# Revit family: ISI_IdealStandard_CounterTopWashbasins_Strada
name_source: partatom
category: Plumbing Fixtures
revit_build: Autodesk Revit MEP 2012 (Build: 20110309_2315(x64)
units: mm (PartAtom-declared; Revit-internal decimal feet)

## types (3) — shared parameters
Accessories = www.idealspec.co.uk
AreaUnits = millimeters
Assembly Code = C1030220
AssetType = Fixed
BREEAM = No
BasinMaterial = ISI_IdealStandard_Sanitaryware_White6_Render
Brand = Ideal Standard
Category = SanitaryTerminal_WASHHANDBASIN_UK
Color = White
ConnectionType = Plumbing
Default Elevation = 1219 mm
DrainSize = 32 mm  [stored 0.104987 ft]
DurationUnit = year
ECA = No
ExpectedLife = 30
Features = Single tap hole, overflow, contemporary design
Finish = White
IfcExportAs = IfcSanitaryTerminalType
IfcExportType = WASHHANDBASIN
InstallationInstructions = www.idealspec.co.uk/resources.html
LinearUnits = millimeters
ManufacturerURL = www.idealspec.co.uk
Material = Vitreous china
NBSDescription = Counter top washbasins
NBSReference = 45-35-70/360
NominalHeight = 130 mm  [stored 0.426509 ft]
NominalWidth = 420 mm
Shape = Rectangular
Space = Internal
SpareParts = www.fastpart-spares.co.uk
TMV3 = No
URL = www.idealspec.co.uk
Uniclass2 = Pr_40_20_96_18
Version = 2
VolumeUnits = Litres
WRAS = No
WarrantyDescription = Manufacturers Warranty
WarrantyDurationParts = 99
WarrantyDurationUnit = year
WashHandBasinMounting = CounterTop
WashHandBasinType = HandRinse
WaterEfficientProduct = No
zero-valued in all types: CWFU, HWFU, WFU

## per-type parameters (varying)
| type | BIMObjectName | Description | Model | ModelNumber | ModelReference | Name | NettWeight | NominalDepth | NominalLength | ProductInformation | Size | WasteCentreLine |
| K077701 - Ideal Standard Strada 50cm Countertop Basin | ISI_IdealStandard_CounterTopWashbasins_Strada_K0777 | Strada 50 cm countertop basin one taphole | K077701 | K077701 | Strada 50 cm countertop basin one taphole | CounterTopWashBasins_Strada_K0777_IdealStandard | 13 Kg | 500 mm | 500 mm | www.idealspec.co.uk/assets/datasheet/K077701 | 500 x 420 x 145 mm | 210 mm |
| K077801 - Ideal Standard Strada 60cm Countertop Basin | ISI_IdealStandard_CounterTopWashbasins_Strada_K0778 | Strada 60 cm countertop basin one taphole | K077801 | K077801 | Strada 60 cm countertop basin one taphole | CounterTopWashBasins_Strada_K0778_IdealStandard | 15 Kg | 600 mm | 600 mm | www.idealspec.co.uk/assets/datasheet/K077801 | 600 x 420 x 145 mm | 210 mm |
| K078201 - Ideal Standard Strada 70cm Countertop Basin | ISI_IdealStandard_CounterTopWashbasins_Strada_K0782 | Strada 70 cm countertop basin one taphole | K078201 | K078201 | Strada 70 cm countertop basin one taphole | CounterTopWashBasins_Strada_K0782_IdealStandard | 17 Kg | 700 mm  [stored 2.29659 ft] | 700 mm  [stored 2.29659 ft] | www.idealspec.co.uk/assets/datasheet/K078201 | 700 x 420 x 150 mm | 225 mm  [stored 0.738189 ft] |

note: [stored X ft] marks values corroborated as IEEE doubles in the binary element streams (Revit-internal decimal feet)

## geometry (parser evidence)
native form markers: Sweep x5
no freeform markers — native parametric forms only
